# Revit family: Maxlogic yangın alarm buton
name_source: partatom
category: Fire Alarm Devices
units: mm (PartAtom-declared; Revit-internal decimal feet)

## family parameters
Cut with Voids When Loaded = No
Host = Face
Maintain Annotation Orientation = Yes
OmniClass Number = 23.85.30.21
OmniClass Title = Environmental Detection/Registration
Part Type = Normal
Room Calculation Point = No
Round Connector Dimension = Use Diameter
Shared = No

## types (3) — shared parameters
Code Performance = EN 54-11
Color = Kırmızı
Fax Number = (+)90 216 466 45 10
Installation Manual = https://mavilielektronik.com
Main Material = Red Plastic ABS
Manufacturer = Mavili Elektronik Ticaret A.Ş.
Model = MaxLogic
Mounting height = Zeminden 1,4m yukarıda (+/-200mm)
Mounting surface = Duvara montaj
Nominal  Width = 87 mm
Nominal Depth = 58 mm
Nominal Height = 91 mm
Operating temperature = (-10°C) - (+55°C)
Operatonal Voltage (default) = 24 V/DC
Protection Sign = IP22D
Protective Cover = ML-0710
Secondary Material = Plastic
URL = https://www.mavili.com.tr
Warranty Duration Labor = 2
Warranty Duration Parts = 2
Warranty Duration Unit = Year
zero-valued in all types: Cost, Default Elevation

## per-type parameters (varying)
| type | Button LED | Description | Device Adress Setup | Operating voltage range | Product Code | Public Works Pose Number | Weight |
| Maxlogic Konvansiyonel Yangın Alarm Butonu Resetlenebilir | No | Konvansiyonel Yangın Alarm Butonu Resetlenebilir |  | 10-30 V/DC | ML-2710 | 830-102 | 140 gr. |
| Maxlogic Adresli Yangın Alarm Butonu Resetlenebilir | Yes | Adresli yangın alarm butonu | El Tipi Adresleme Cihazı | 18-33 V/DC | ML-1710 | 833-557 | 150 gr. |
| Maxlogic Adresli Yangın Alarm Butonu Resetlenebilir, Kısa Devre İzolatörlü | Yes | Adresli yangın alarm butonu (Kısa devre izolatörlü) | El Tipi Adresleme Cihazı | 10-30 V/DC | ML-1710.SCI | 833-558 | 150 gr. |

## geometry (parser evidence)
native form markers: Sweep x3
no freeform markers — native parametric forms only
